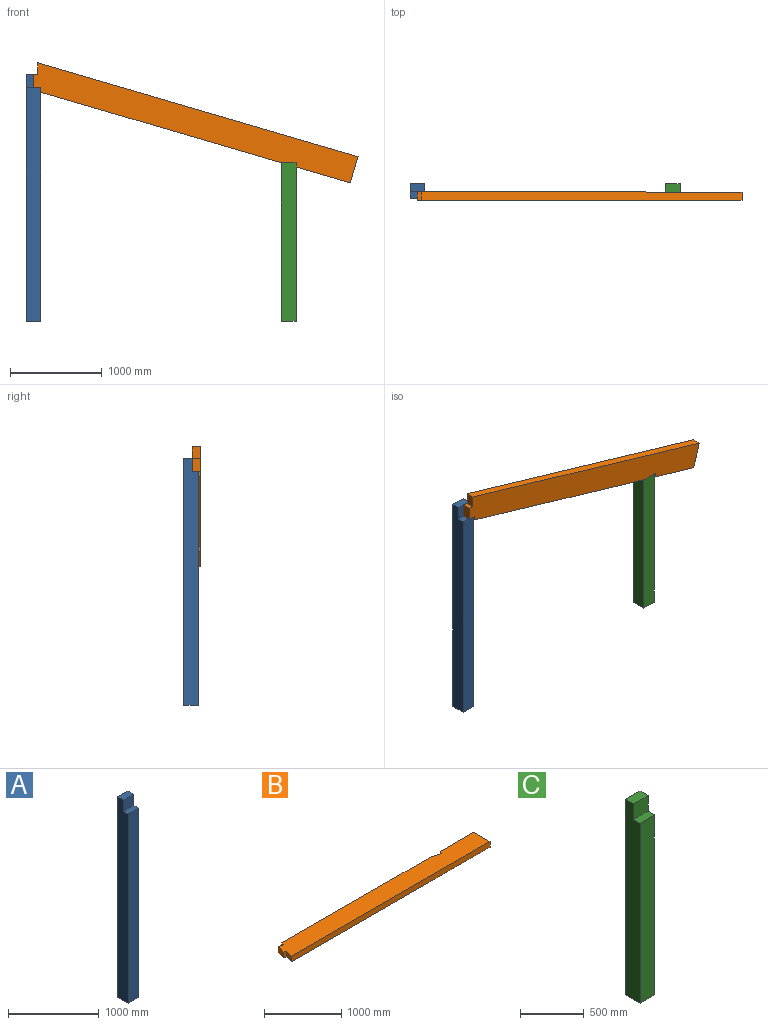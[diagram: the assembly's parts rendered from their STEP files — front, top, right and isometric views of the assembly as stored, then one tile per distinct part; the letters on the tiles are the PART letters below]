
ASSEMBLY  parts=3 mates=2
PART A: 8 faces, bbox 160x160x2700 mm
  f0: plane 2550x160mm, normal (0,-1,0), area 408000mm2, adj f1,f3,f5,f6
  f1: plane 2700x160mm, normal (-1,0,0), area 421500mm2, adj f0,f2,f4,f5,f6,f7
  f2: plane 2700x160mm, normal (0,1,0), area 432000mm2, adj f1,f3,f4,f5
  f3: plane 2700x160mm, normal (1,0,0), area 421500mm2, adj f0,f2,f4,f5,f6,f7
  f4: plane 160x90mm, normal (0,0,1), area 14400mm2, adj f1,f2,f3,f7
  f5: plane 160x160mm, normal (0,0,-1), area 25600mm2, adj f0,f1,f2,f3
  f6: plane 160x70mm, normal (0,0,1), area 11200mm2, adj f0,f1,f3,f7
  f7: plane 160x150mm, normal (0,-1,0), area 24000mm2, adj f1,f3,f4,f6
PART B: 13 faces, bbox 3655x300x90 mm
  f0: plane 3654.97x300mm, normal (0,0,-1), area 1082028.3mm2, adj f2,f3,f4,f5,f6,f7,f8,f9
  f1: plane 3654.97x300mm, normal (0,0,1), area 1082028.3mm2, adj f2,f3,f4,f5,f6,f7,f8,f9
  f2: plane 616.7x90mm, normal (0,1,0), area 55503.2mm2, adj f0,f1,f6,f11
  f3: plane 3643.57x90mm, normal (0,-1,0), area 327921.3mm2, adj f0,f1,f6,f10
  f4: plane 138.74x90mm, normal (-0.96,0.28,0), area 13012.8mm2, adj f0,f1,f7,f9
  f5: plane 2742.5x90mm, normal (0,1,0), area 246825.4mm2, adj f0,f1,f8,f12
  f6: plane 300x90mm, normal (1,0,0), area 27000mm2, adj f0,f1,f2,f3
  f7: plane 90x76.76mm, normal (0.28,0.96,0), area 7200mm2, adj f0,f1,f4,f8
  f8: plane 90x45.05mm, normal (-0.96,0.28,0), area 4225.7mm2, adj f0,f1,f5,f7
  f9: plane 90x47.98mm, normal (-0.28,-0.96,0), area 4500mm2, adj f0,f1,f4,f10
  f10: plane 124.66x90mm, normal (-0.96,0.28,0), area 11692.3mm2, adj f0,f1,f3,f9
  f11: plane 90x45.92mm, normal (-0.96,0.29,0), area 4319.6mm2, adj f0,f1,f2,f12
  f12: plane 151.11x90mm, normal (0.29,0.96,0), area 14213.7mm2, adj f0,f1,f5,f11
PART C: 8 faces, bbox 160x160x1880 mm
  f0: plane 1880x160mm, normal (1,0,0), area 290300mm2, adj f2,f3,f4,f5,f6,f7
  f1: plane 1880x160mm, normal (-1,0,0), area 290300mm2, adj f2,f3,f4,f5,f6,f7
  f2: plane 1880x160mm, normal (0,1,0), area 300800mm2, adj f0,f1,f4,f5
  f3: plane 1730x160mm, normal (0,-1,0), area 276800mm2, adj f0,f1,f5,f6
  f4: plane 160x90mm, normal (0,0,1), area 14400mm2, adj f0,f1,f2,f7
  f5: plane 160x160mm, normal (0,0,-1), area 25600mm2, adj f0,f1,f2,f3
  f6: plane 160x70mm, normal (0,0,1), area 11200mm2, adj f0,f1,f3,f7
  f7: plane 160x150mm, normal (0,-1,0), area 24000mm2, adj f0,f1,f4,f6
PLACE A t=(-3051.74,699.95,-258.41)mm
PLACE B rot(axis=(-0.98,0.14,0.14),91.2deg) t=(-2486.14,689.95,2610.13)mm
PLACE C t=(404.19,699.95,-258.34)mm
MATE parallel C.f0 <-> A.f1  axis (1,0,0) through (484.19,699.95,-258.34)mm
MATE parallel B.f7 <-> A.f6  axis (0,0,-1) through (-2306.04,689.95,2291.58)mm
